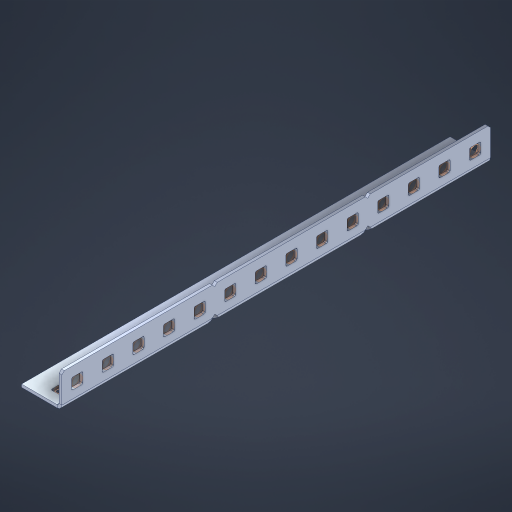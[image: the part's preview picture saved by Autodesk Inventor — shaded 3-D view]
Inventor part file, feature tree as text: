
AUTODESK INVENTOR PART (.ipt)
format: ipt  version: 2023 (Build 270158000, 158)  size: 634,880 bytes
history: native  units: in
note: dims shown in document units (in); Inventor stores cm internally (conversion verified against a paired STEP export)
features: other x33, extrude x27, sheet_metal_op x10, sketch x8, mirror x1, pattern_linear x1, chamfer x1
ambient origin geometry x8: Origin, YZ Plane, XZ Plane, XY Plane, X Axis, Y Axis, Z Axis, Center Point
bodies: Solid1 (feature_tree), Body (feature_tree)
feature tree (81):
  other  "Flange Pattern Plane"
  sheet_metal_op  "Flange Pattern"
  sheet_metal_op  "Body Pattern"
  other  "Arc Length"
  mirror  "Notch Mirror"
  pattern_linear  "Notch Pattern"  Spacing1=0.1875in  [1 undecoded]
  chamfer  "End Chamfer"
  extrude  "Half Cut"  Depth=0.0469in
  sketch  "Sketch1"  dims[d0=2.5in]
  other  "Plate1"
  sketch  "Sketch2"  dims[d1=7.0in]
  other  "Plate2"
  sheet_metal_op  "Bend1"
  sheet_metal_op  "Corner1"
  sketch  "Sketch3"  dims[d2=0.0469in]
  other  "Flange Pattern Sketch"
  sketch  "Sketch7"  dims[d3=0.0469in]
  other  "Srf1"
  other  "Srf2"
  sketch  "Sketch8"  dims[d4=0.0234in]
  sketch  "Sketch9"  dims[d5=0.0938in]
  other  "Srf91"
  sheet_metal_op  "Body Pattern Sketch"
  other  "Srf92"
  sketch  "Sketch13"  dims[d6=0.0469in]
  sketch  "Sketch14"  dims[d7=0.5in d8=90.0deg d9=0.0312in d10=0.1875in d11=0.0469in d12=0.0469in d16=0.182in d17=0.02in d18=0.0469in d19=0.0in d20=0.25in d21=0.25in d46=0.172in d47=1.0in d48=0.0in d49=0.182in d50=0.02in d51=0.25in d52=0.25in d53=0.0469in d54=0.0in d55=0.172in d56=1.0in d57=0.0in d60=5.5118in d62=0.5in d63=0.3937in d65=0.5in d85=0.1227in d86=0.1659in d88=0.04in d89=0.0469in d90=0.0in d91=0.04in d92=0.0491in d95=2.5in d96=0.04in d97=0.25in d98=45.0deg d101=0.0in d102=2.497in d131=0.5in d132=5.5118in d134=0.5in d139=0.5in]
  other  "Srf856"
  other  "Srf1310"
  other  "Srf1311"
  other  "Srf1312"
  other  "Srf1376"
  other  "Srf1377"
  other  "Srf1728"
  other  "Srf1755"
  other  "Srf1878"
  other  "Srf1879"
  other  "Srf1880"
  other  "Srf1881"
  other  "Srf1882"
  other  "Srf1883"
  other  "Srf1884"
  other  "Srf1885"
  other  "Srf1942"
  other  "Srf1943"
  other  "Srf1944"
  other  "Srf1945"
  other  "Srf1946"
  other  "Srf1947"
  other  "Srf1948"
  other  "Srf1949"
  sheet_metal_op  "Flange Stamp"
  sheet_metal_op  "Flange Circle"
  sheet_metal_op  "Body Stamp"
  sheet_metal_op  "Body Circle"
  sheet_metal_op  "Notch"
  extrude  "ExtrusionSrf2"  Depth=0.0469in
  extrude  "ExtrusionSrf92"  Depth=0.5in
  extrude  "ExtrusionSrf856"  Depth=0.02in
  extrude  "ExtrusionSrf1310"  Depth=0.0469in
  extrude  "ExtrusionSrf1311"  TaperAngle=0.0deg  [1 undecoded]
  extrude  "ExtrusionSrf1312"  Depth=0.5in
  extrude  "ExtrusionSrf1376"  Depth=0.5in
  extrude  "ExtrusionSrf1377"  Depth=0.5in
  extrude  "ExtrusionSrf1728"  Depth=0.5in TaperAngle=0.0deg
  extrude  "ExtrusionSrf1755"  Depth=0.5in
  extrude  "ExtrusionSrf1878"  Depth=0.02in
  extrude  "ExtrusionSrf1879"  Depth=0.5in
  extrude  "ExtrusionSrf1880"  Depth=0.5in
  extrude  "ExtrusionSrf1881"  Depth=0.0469in
  extrude  "ExtrusionSrf1882"  TaperAngle=0.0deg  [1 undecoded]
  extrude  "ExtrusionSrf1883"  Depth=0.5in
  extrude  "ExtrusionSrf1884"  Depth=0.5in TaperAngle=0.0deg
  extrude  "ExtrusionSrf1885"  Depth=0.5in
  extrude  "ExtrusionSrf1942"  Depth=0.5in
  extrude  "ExtrusionSrf1943"  Depth=0.5in
  extrude  "ExtrusionSrf1944"  Depth=0.5in
  extrude  "ExtrusionSrf1945"  Depth=0.5in
  extrude  "ExtrusionSrf1946"  Depth=0.0469in
  extrude  "ExtrusionSrf1947"  TaperAngle=0.0deg  [1 undecoded]
  extrude  "ExtrusionSrf1948"  Depth=0.5in
  extrude  "ExtrusionSrf1949"  Depth=0.5in
note: 4 required parameter values undecoded (feature->parameter linkage not recoverable at this tier; creation-order binding heuristic only, values carry confidence <= 0.55)
